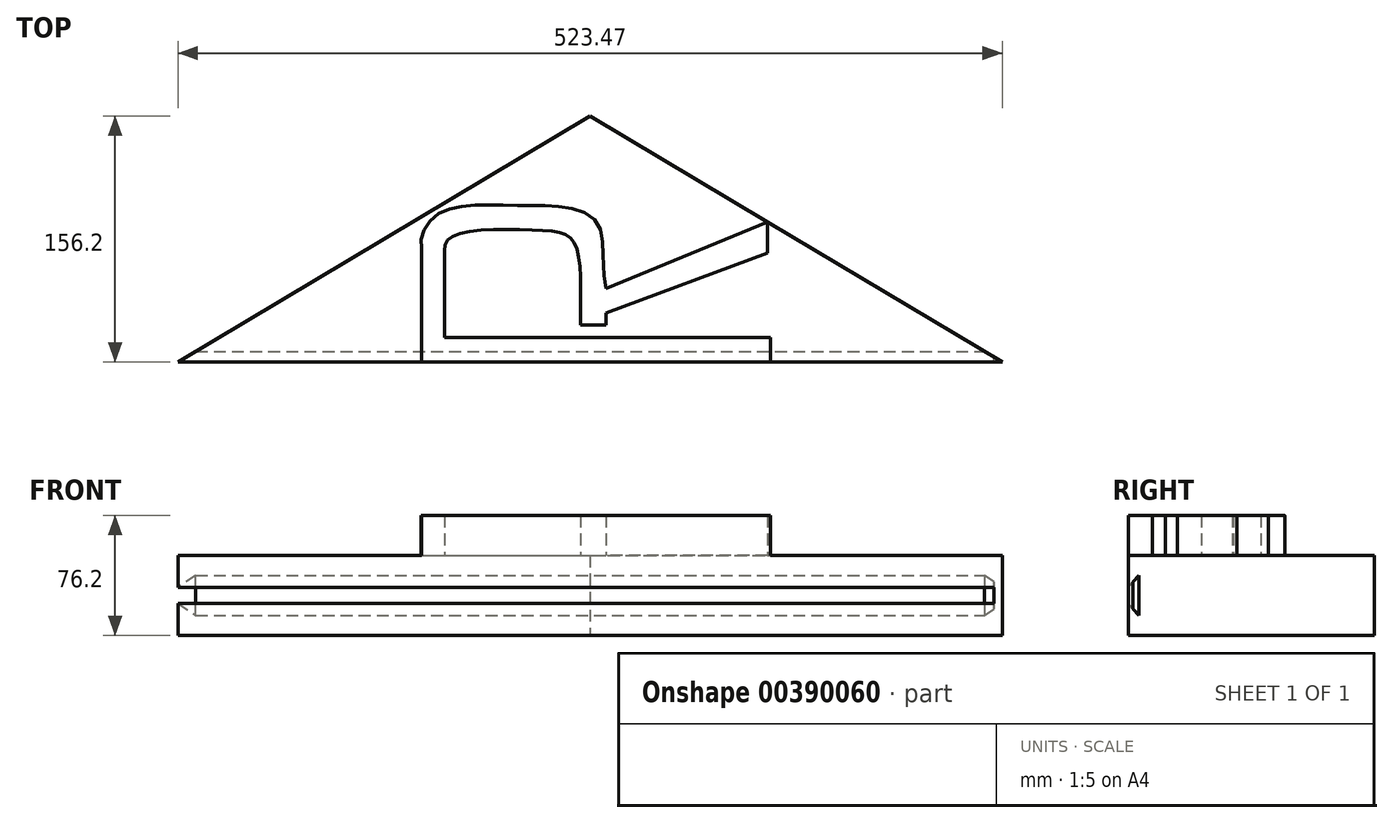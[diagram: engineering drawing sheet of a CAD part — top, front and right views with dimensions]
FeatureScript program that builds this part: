
annotation { "Feature Type Name" : "Feature", "Feature Type Description" : "" }
export const myFeature = defineFeature(function(context is Context, id is Id, definition is map)
    precondition{}
    {
        {
            var Q0;
            Q0=qCreatedBy(makeId("Top.planeOp"),FACE);
            var sketch = newSketch(context, id + "F0", { "sketchPlane" : qUnion([Q0])});
            skLineSegment(sketch, "E0", {"start": v(-518.22, 0) * mm, "end": v(5.25, 0) * mm});
            skLineSegment(sketch, "E1", {"start": v(-518.22, 0) * mm, "end": v(-256.48, 156.2) * mm});
            skLineSegment(sketch, "E2", {"start": v(-256.48, 156.2) * mm, "end": v(5.25, 0) * mm});
            skSolve(sketch);
        }
        {
            var Q0;
            Q0=makeQuery(id+"F0.imprint","IMPRINT",FACE,{"disambiguationData":[TD([[makeQuery(id+"F0.imprint","IMPRINT",EDGE,{"derivedFrom":sQuery(id+"F0.wireOp",EDGE,"E0")}),1.0]])]});
            extrude(context, id + "F1", {"entities" : qUnion([Q0]), "depth" : 50.8 * mm});
        }
        {
            var Q0;
            Q0=qCreatedBy(makeId("Right.planeOp"),FACE);
            var sketch = newSketch(context, id + "F2", { "sketchPlane" : qUnion([Q0])});
            skLineSegment(sketch, "E3", {"start": v(0, 30.48) * mm, "end": v(6.72, 38.1) * mm});
            skLineSegment(sketch, "E4", {"start": v(6.72, 38.1) * mm, "end": v(6.72, 12.7) * mm});
            skLineSegment(sketch, "E5", {"start": v(6.72, 12.7) * mm, "end": v(0, 20.32) * mm});
            skLineSegment(sketch, "E6", {"start": v(0, 20.32) * mm, "end": v(0, 30.48) * mm});
            skSolve(sketch);
        }
        {
            var Q0;
            Q0=makeQuery(id+"F2.imprint","IMPRINT",FACE,{"disambiguationData":[TD([[makeQuery(id+"F2.imprint","IMPRINT",EDGE,{"derivedFrom":sQuery(id+"F2.wireOp",EDGE,"E3")}),-1.0]])]});
            extrude(context, id + "F3", {"entities" : qUnion([Q0]), "operationType" : NewBodyOperationType.REMOVE, "endBound" : BoundingType.THROUGH_ALL, "oppositeDirection" : true, "depth" : 25.4 * mm});
        }
        {
            var Q0;
            Q0=makeQuery(id+"F1.opExtrude","CAP_FACE",FACE,{"disambiguationData":[OSD([sQuery(id+"F0.wireOp",EDGE,"E0"),sQuery(id+"F0.wireOp",EDGE,"E1"),sQuery(id+"F0.wireOp",EDGE,"E2")])],"isStart":false});
            var sketch = newSketch(context, id + "F4", { "sketchPlane" : qUnion([Q0])});
            skLineSegment(sketch, "E7.bottom", {"start": v(-363.56, 0) * mm, "end": v(-141.86, 0) * mm});
            skLineSegment(sketch, "E7.top", {"start": v(-363.56, 15.44) * mm, "end": v(-141.86, 15.44) * mm});
            skLineSegment(sketch, "E7.left", {"start": v(-363.56, 0) * mm, "end": v(-363.56, 15.44) * mm});
            skLineSegment(sketch, "E7.right", {"start": v(-141.86, 0) * mm, "end": v(-141.86, 15.44) * mm});
            skLineSegment(sketch, "E8", {"start": v(-348.96, 15.44) * mm, "end": v(-348.96, 66.76) * mm});
            skLineSegment(sketch, "E9", {"start": v(-262.49, 23.59) * mm, "end": v(-246.5, 23.59) * mm});
            skLineSegment(sketch, "E10", {"start": v(-246.5, 23.59) * mm, "end": v(-246.5, 31.22) * mm});
            skLineSegment(sketch, "E11", {"start": v(-246.5, 31.22) * mm, "end": v(-143.94, 69.14) * mm});
            skLineSegment(sketch, "E12", {"start": v(-143.94, 69.14) * mm, "end": v(-143.94, 89.03) * mm});
            skLineSegment(sketch, "E13", {"start": v(-143.94, 89.03) * mm, "end": v(-246.5, 46.6) * mm});
            skLineSegment(sketch, "E14", {"start": v(-262.49, 23.59) * mm, "end": v(-262.49, 40.77) * mm});
            skFitSpline(sketch, "E15", {"points": [v(-348.96, 66.76) * mm, v(-344.62, 79.39) * mm, v(-288.4, 83.59) * mm, v(-267.42, 76.96) * mm, v(-262.49, 40.77) * mm], "startDerivative": vector(-4.27, 96.51) * mm, "endDerivative": vector(-0.93, -160.44) * mm});
            skLineSegment(sketch, "E16", {"start": v(-363.56, 15.44) * mm, "end": v(-363.56, 66.07) * mm});
            skFitSpline(sketch, "E17", {"points": [v(-363.56, 66.07) * mm, v(-363.56, 79.17) * mm, v(-354.1, 93.34) * mm, v(-332.46, 99.39) * mm, v(-302.1, 99.37) * mm, v(-273.36, 98.37) * mm, v(-252.22, 88.73) * mm, v(-248.28, 66.07) * mm, v(-246.5, 46.6) * mm], "startDerivative": vector(8.47, 169.03) * mm, "endDerivative": vector(32.44, -227.03) * mm});
            skSolve(sketch);
        }
        {
            var Q0;
            {var subQ2=sQuery(id+"F4.wireOp",EDGE,"E8");Q0=makeQuery(id+"F4.imprint","IMPRINT",FACE,{"disambiguationData":[TD([[makeQuery(id+"F4.imprint","IMPRINT",EDGE,{"derivedFrom":subQ2}),1.0]])]});}
            var Q1;
            Q1=makeQuery(id+"F4.imprint","IMPRINT",FACE,{"disambiguationData":[TD([[makeQuery(id+"F4.imprint","IMPRINT",EDGE,{"derivedFrom":sQuery(id+"F4.wireOp",EDGE,"E7.bottom")}),1.0]])]});
            extrude(context, id + "F5", {"entities" : qUnion([Q0, Q1]), "operationType" : NewBodyOperationType.ADD, "depth" : 25.4 * mm});
        }
    });
